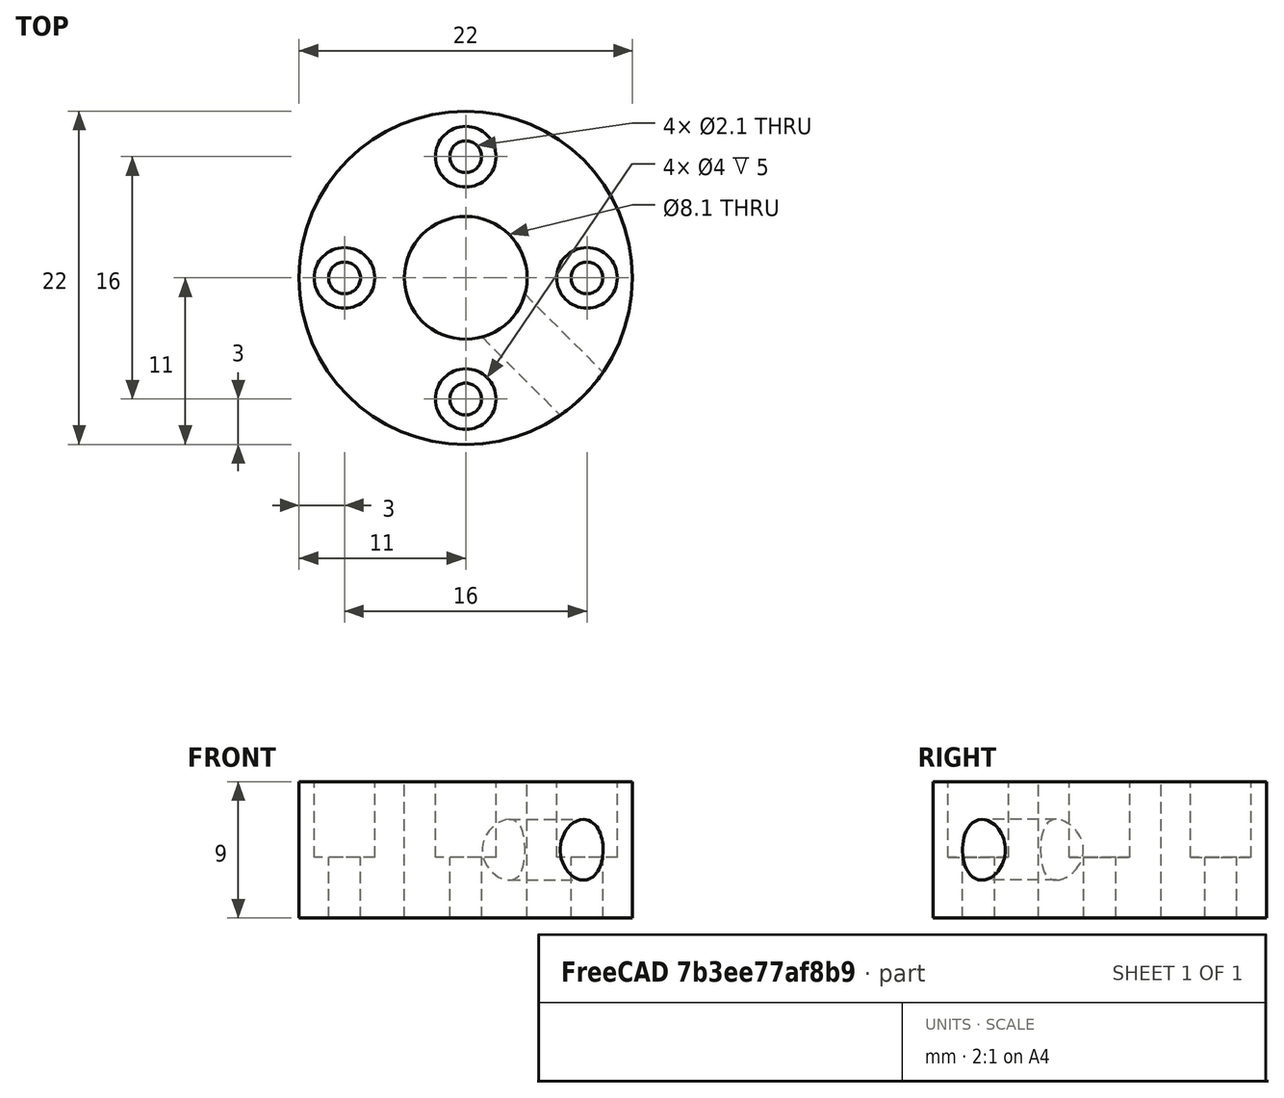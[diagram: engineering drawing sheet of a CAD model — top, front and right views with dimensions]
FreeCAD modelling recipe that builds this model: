
FCSTD DOCUMENT  (FreeCAD 0.17R13541 (Git))
Label: AX-12-Coupler
License: All rights reserved
LicenseURL: http://en.wikipedia.org/wiki/All_rights_reserved
objects: Part::Cylinder×11, Part::Cut×6, Part::MultiFuse×4
note: 21 computed .brp shape members not serialized (recipe doc carries the construction recipe); baked Part::Feature solids carry a one-line shape summary decoded from their .brp

FEATURE [Part::Cylinder] Cylinder
  Angle = 360
  AttacherType = Attacher::AttachEngine3D
  Height = 9
  Radius = 11
FEATURE [Part::Cylinder] Cylinder001
  Angle = 360
  AttacherType = Attacher::AttachEngine3D
  Height = 10
  Placement = pos=(8,0,0) rot=(0,0,1;0rad)
  Radius = 1.05
FEATURE [Part::Cylinder] Cylinder005
  Angle = 360
  AttacherType = Attacher::AttachEngine3D
  Height = 10
  Radius = 4.05
FEATURE [Part::Cylinder] Cylinder006
  Angle = 360
  AttacherType = Attacher::AttachEngine3D
  Height = 10
  Placement = pos=(8,0,5) rot=(0,0,1;0rad)
  Radius = 2
FEATURE [Part::MultiFuse] Fusion
  Placement = pos=(0,0,-1) rot=(0,0,1;0rad)
  Shapes = -> [Cylinder001,Cylinder006]
FEATURE [Part::Cylinder] Cylinder007
  Angle = 360
  AttacherType = Attacher::AttachEngine3D
  Height = 10
  Placement = pos=(8,0,5) rot=(0,0,1;0rad)
  Radius = 2
FEATURE [Part::Cylinder] Cylinder008
  Angle = 360
  AttacherType = Attacher::AttachEngine3D
  Height = 10
  Placement = pos=(8,0,0) rot=(0,0,1;0rad)
  Radius = 1.05
FEATURE [Part::MultiFuse] Fusion001
  Placement = pos=(-16,0,-1) rot=(0,0,1;0rad)
  Shapes = -> [Cylinder008,Cylinder007]
FEATURE [Part::Cylinder] Cylinder009
  Angle = 360
  AttacherType = Attacher::AttachEngine3D
  Height = 10
  Placement = pos=(8,0,5) rot=(0,0,1;0rad)
  Radius = 2
FEATURE [Part::Cylinder] Cylinder010
  Angle = 360
  AttacherType = Attacher::AttachEngine3D
  Height = 10
  Placement = pos=(8,0,0) rot=(0,0,1;0rad)
  Radius = 1.05
FEATURE [Part::MultiFuse] Fusion002
  Placement = pos=(-8,8,-1) rot=(0,0,1;0rad)
  Shapes = -> [Cylinder010,Cylinder009]
FEATURE [Part::Cylinder] Cylinder011
  Angle = 360
  AttacherType = Attacher::AttachEngine3D
  Height = 10
  Placement = pos=(8,0,5) rot=(0,0,1;0rad)
  Radius = 2
FEATURE [Part::Cylinder] Cylinder012
  Angle = 360
  AttacherType = Attacher::AttachEngine3D
  Height = 10
  Placement = pos=(8,0,0) rot=(0,0,1;0rad)
  Radius = 1.05
FEATURE [Part::MultiFuse] Fusion003
  Placement = pos=(-8,-8,-1) rot=(0,0,1;0rad)
  Shapes = -> [Cylinder012,Cylinder011]
FEATURE [Part::Cylinder] Cylinder013
  Angle = 360
  AttacherType = Attacher::AttachEngine3D
  Height = 12
  Placement = pos=(0,0,4.5) rot=(0.707107,0.707107,0;1.5708rad)
  Radius = 2
FEATURE [Part::Cut] Cut
  Base = -> Cylinder
  Tool = -> Fusion
FEATURE [Part::Cut] Cut001
  Base = -> Cut
  Tool = -> Fusion001
FEATURE [Part::Cut] Cut002
  Base = -> Cut001
  Tool = -> Fusion002
FEATURE [Part::Cut] Cut003
  Base = -> Cut002
  Tool = -> Fusion003
FEATURE [Part::Cut] Cut004
  Base = -> Cut003
  Tool = -> Cylinder005
FEATURE [Part::Cut] Cut005
  Base = -> Cut004
  Tool = -> Cylinder013
